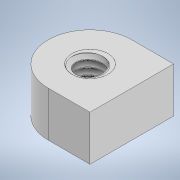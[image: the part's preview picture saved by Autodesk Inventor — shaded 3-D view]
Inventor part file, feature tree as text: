
AUTODESK INVENTOR PART (.ipt)
format: ipt  version: 2022.2 (Build 262287000, 287)  size: 673,280 bytes
history: native  units: mm
features: sketch x4, other x3, projected_geometry x2, hole x1, thread x1, revolve x1, helix x1, extrude x1
ambient origin geometry x8: Origin, YZ Plane, XZ Plane, XY Plane, X Axis, Y Axis, Z Axis, Center Point
bodies: Solid2 (feature_tree), Solid1 (feature_tree)
feature tree (14):
  other  "Bending Tool.ipt"
  hole  "Hole1"  [1 undecoded]
  thread  "Thread1"  [1 undecoded]
  revolve  "Revolution1"  [1 undecoded]
  helix  "Coil1"  [1 undecoded]
  extrude  "Extrusion1"  Depth=10.0mm TaperAngle=0.0deg
  other  "Solid1::Bending Tool.ipt"
  other  "TaggingFeature1"
  sketch  "Sketch1"  dims[d0=10.0mm]
  sketch  "Sketch2"  dims[d1=2.15mm d2=6.0mm d3=6.0mm d4=3.0mm d5=90.0deg d6=8.0mm d7=0.0mm d8=3.7mm d9=0.0mm d10=9.599311mm d11=0.064033mm d12=0.064033mm]
  sketch  "Sketch3"  dims[d15=0.4mm d17=9.599311mm d19=0.0mm]
  sketch  "Sketch4"  dims[d20=0.4004mm d21=4.5mm d22=10.0mm d23=0.0mm d24=0.0mm d25=0.0mm d26=0.0mm d27=0.0mm d28=1.0mm d29=0.0mm]
  projected_geometry  "Projected Loop1"
  projected_geometry  "Projected Loop2"
note: 4 required parameter values undecoded (feature->parameter linkage not recoverable at this tier; creation-order binding heuristic only, values carry confidence <= 0.55)